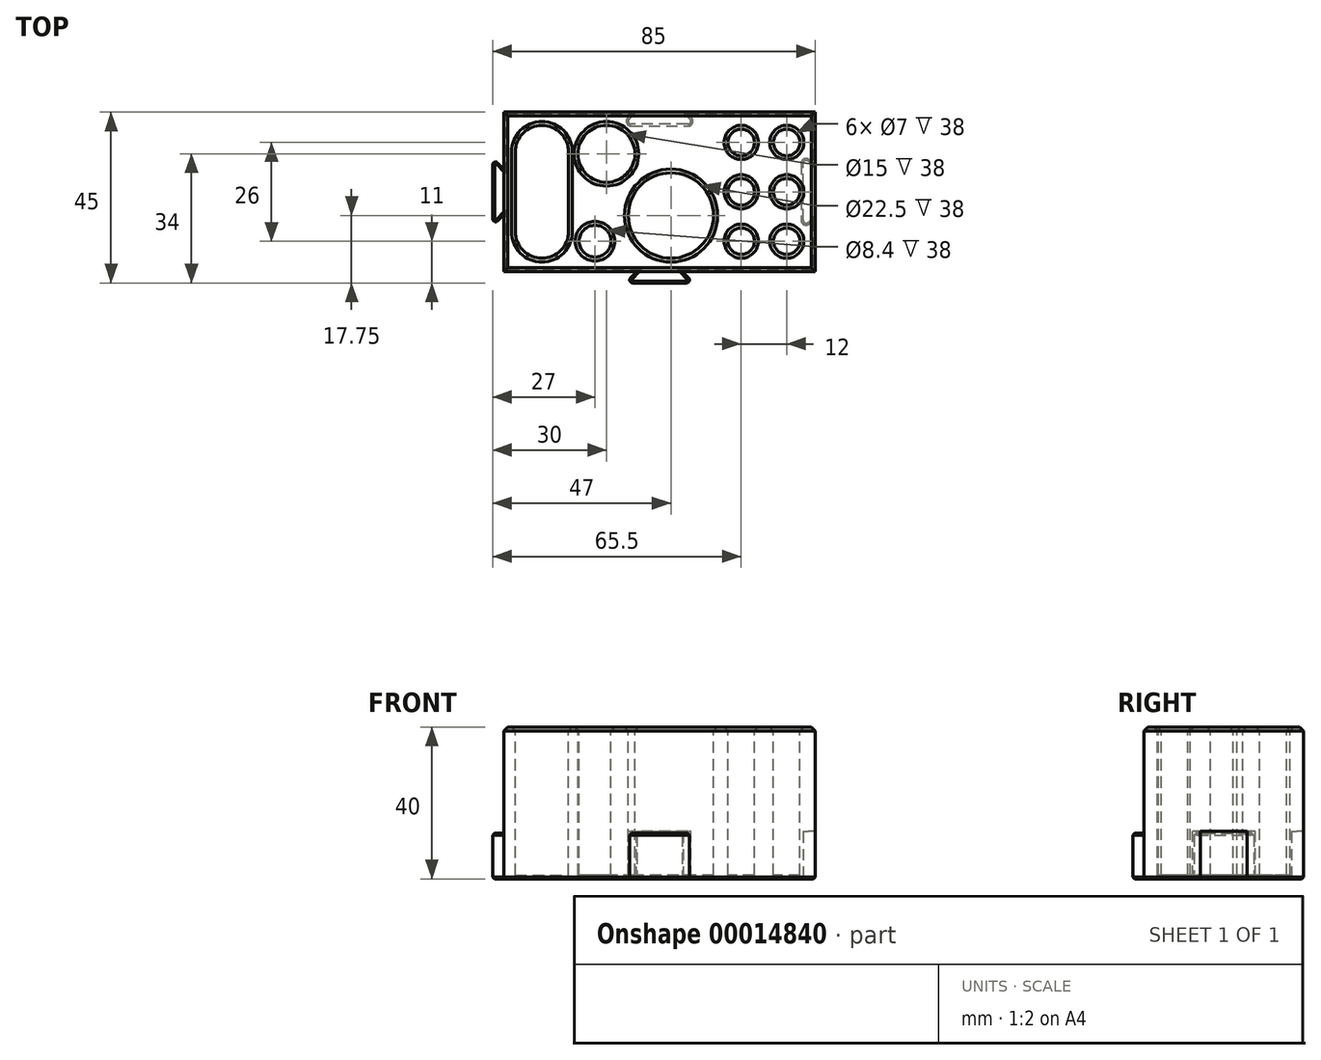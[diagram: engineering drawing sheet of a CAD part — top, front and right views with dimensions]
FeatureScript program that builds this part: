
annotation { "Feature Type Name" : "Feature", "Feature Type Description" : "" }
export const myFeature = defineFeature(function(context is Context, id is Id, definition is map)
    precondition{}
    {
        {
            var Q0;
            Q0=qCreatedBy(makeId("Top.planeOp"),FACE);
            var sketch = newSketch(context, id + "F0", { "sketchPlane" : qUnion([Q0])});
            skLineSegment(sketch, "E0.bottom", {"start": v(0, 0) * mm, "end": v(82, 0) * mm});
            skLineSegment(sketch, "E0.top", {"start": v(0, 42) * mm, "end": v(82, 42) * mm});
            skLineSegment(sketch, "E0.left", {"start": v(0, 0) * mm, "end": v(0, 42) * mm});
            skLineSegment(sketch, "E0.right", {"start": v(82, 0) * mm, "end": v(82, 42) * mm});
            skLineSegment(sketch, "E1", {"start": v(0, 21) * mm, "end": v(82, 21) * mm, "construction": true});
            skLineSegment(sketch, "E2", {"start": v(41, 42) * mm, "end": v(41, 0) * mm, "construction": true});
            skLineSegment(sketch, "E3", {"start": v(35, 0) * mm, "end": v(32, -3) * mm});
            skLineSegment(sketch, "E4", {"start": v(32, -3) * mm, "end": v(50, -3) * mm});
            skLineSegment(sketch, "E5", {"start": v(50, -3) * mm, "end": v(47, 0) * mm});
            skLineSegment(sketch, "E6", {"start": v(47.2, 42) * mm, "end": v(50.4, 38.8) * mm});
            skLineSegment(sketch, "E7", {"start": v(50.4, 38.8) * mm, "end": v(31.6, 38.8) * mm});
            skLineSegment(sketch, "E8", {"start": v(31.6, 38.8) * mm, "end": v(34.8, 42) * mm});
            skLineSegment(sketch, "E9", {"start": v(0, 15) * mm, "end": v(-3, 12) * mm});
            skLineSegment(sketch, "E10", {"start": v(-3, 12) * mm, "end": v(-3, 30) * mm});
            skLineSegment(sketch, "E11", {"start": v(-3, 30) * mm, "end": v(0, 27) * mm});
            skLineSegment(sketch, "E12", {"start": v(82, 14.8) * mm, "end": v(78.8, 11.6) * mm});
            skLineSegment(sketch, "E13", {"start": v(78.8, 11.6) * mm, "end": v(78.8, 30.4) * mm});
            skLineSegment(sketch, "E14", {"start": v(78.8, 30.4) * mm, "end": v(82, 27.2) * mm});
            skSolve(sketch);
        }
        {
            var Q0;
            {var subQ1=sQuery(id+"F0.wireOp",EDGE,"E6");Q0=makeQuery(id+"F0.imprint","IMPRINT",FACE,{"disambiguationData":[TD([[makeQuery(id+"F0.imprint","IMPRINT",EDGE,{"derivedFrom":subQ1}),-1.0]])]});}
            var Q1;
            {var subQ1=sQuery(id+"F0.wireOp",EDGE,"E12");Q1=makeQuery(id+"F0.imprint","IMPRINT",FACE,{"disambiguationData":[TD([[makeQuery(id+"F0.imprint","IMPRINT",EDGE,{"derivedFrom":subQ1}),-1.0]])]});}
            var Q2;
            {var subQ8=sQuery(id+"F0.wireOp",EDGE,"E6");Q2=makeQuery(id+"F0.imprint","IMPRINT",FACE,{"disambiguationData":[TD([[makeQuery(id+"F0.imprint","IMPRINT",EDGE,{"derivedFrom":subQ8}),1.0]])]});}
            extrude(context, id + "F1", {"entities" : qUnion([Q0, Q1, Q2]), "depth" : 40 * mm});
        }
        {
            var Q0;
            {var subQ1=sQuery(id+"F0.wireOp",EDGE,"E3");Q0=makeQuery(id+"F0.imprint","IMPRINT",FACE,{"disambiguationData":[TD([[makeQuery(id+"F0.imprint","IMPRINT",EDGE,{"derivedFrom":subQ1}),1.0]])]});}
            var Q1;
            {var subQ1=sQuery(id+"F0.wireOp",EDGE,"E9");Q1=makeQuery(id+"F0.imprint","IMPRINT",FACE,{"disambiguationData":[TD([[makeQuery(id+"F0.imprint","IMPRINT",EDGE,{"derivedFrom":subQ1}),-1.0]])]});}
            extrude(context, id + "F2", {"entities" : qUnion([Q0, Q1]), "operationType" : NewBodyOperationType.ADD, "depth" : 12 * mm});
        }
        {
            var Q0;
            {var subQ1=sQuery(id+"F0.wireOp",EDGE,"E6");Q0=makeQuery(id+"F0.imprint","IMPRINT",FACE,{"disambiguationData":[TD([[makeQuery(id+"F0.imprint","IMPRINT",EDGE,{"derivedFrom":subQ1}),-1.0]])]});}
            var Q1;
            {var subQ1=sQuery(id+"F0.wireOp",EDGE,"E12");Q1=makeQuery(id+"F0.imprint","IMPRINT",FACE,{"disambiguationData":[TD([[makeQuery(id+"F0.imprint","IMPRINT",EDGE,{"derivedFrom":subQ1}),-1.0]])]});}
            extrude(context, id + "F3", {"entities" : qUnion([Q0, Q1]), "operationType" : NewBodyOperationType.REMOVE, "depth" : 12.5 * mm});
        }
        {
            var Q0;
            Q0=makeQuery(id+"F3.boolean.opBoolean","COPY",EDGE,{"derivedFrom":makeQuery(id+"F3.opExtrude","SWEPT_EDGE",EDGE,{"disambiguationData":[OSD([sQuery(id+"F0.wireOp",EDGE,"E0.right"),sQuery(id+"F0.wireOp",EDGE,"E14")])]})});
            var Q1;
            Q1=makeQuery(id+"F3.boolean.opBoolean","COPY",EDGE,{"derivedFrom":makeQuery(id+"F3.opExtrude","SWEPT_EDGE",EDGE,{"disambiguationData":[OSD([sQuery(id+"F0.wireOp",EDGE,"E13"),sQuery(id+"F0.wireOp",EDGE,"E14")])]})});
            var Q2;
            Q2=makeQuery(id+"F3.boolean.opBoolean","COPY",EDGE,{"derivedFrom":makeQuery(id+"F3.opExtrude","SWEPT_EDGE",EDGE,{"disambiguationData":[OSD([sQuery(id+"F0.wireOp",EDGE,"E0.right"),sQuery(id+"F0.wireOp",EDGE,"E12")])]})});
            var Q3;
            Q3=makeQuery(id+"F2.opExtrude","SWEPT_EDGE",EDGE,{"disambiguationData":[OSD([sQuery(id+"F0.wireOp",EDGE,"E4"),sQuery(id+"F0.wireOp",EDGE,"E5")])]});
            var Q4;
            Q4=makeQuery(id+"F3.boolean.opBoolean","COPY",EDGE,{"derivedFrom":makeQuery(id+"F3.opExtrude","SWEPT_EDGE",EDGE,{"disambiguationData":[OSD([sQuery(id+"F0.wireOp",EDGE,"E12"),sQuery(id+"F0.wireOp",EDGE,"E13")])]})});
            var Q5;
            Q5=makeQuery(id+"F3.boolean.opBoolean","COPY",EDGE,{"derivedFrom":makeQuery(id+"F3.opExtrude","SWEPT_EDGE",EDGE,{"disambiguationData":[OSD([sQuery(id+"F0.wireOp",EDGE,"E0.top"),sQuery(id+"F0.wireOp",EDGE,"E8")])]})});
            var Q6;
            Q6=makeQuery(id+"F3.boolean.opBoolean","COPY",EDGE,{"derivedFrom":makeQuery(id+"F3.opExtrude","SWEPT_EDGE",EDGE,{"disambiguationData":[OSD([sQuery(id+"F0.wireOp",EDGE,"E0.top"),sQuery(id+"F0.wireOp",EDGE,"E6")])]})});
            var Q7;
            Q7=makeQuery(id+"F3.boolean.opBoolean","COPY",EDGE,{"derivedFrom":makeQuery(id+"F3.opExtrude","SWEPT_EDGE",EDGE,{"disambiguationData":[OSD([sQuery(id+"F0.wireOp",EDGE,"E7"),sQuery(id+"F0.wireOp",EDGE,"E8")])]})});
            var Q8;
            Q8=makeQuery(id+"F3.boolean.opBoolean","COPY",EDGE,{"derivedFrom":makeQuery(id+"F3.opExtrude","SWEPT_EDGE",EDGE,{"disambiguationData":[OSD([sQuery(id+"F0.wireOp",EDGE,"E6"),sQuery(id+"F0.wireOp",EDGE,"E7")])]})});
            var Q9;
            Q9=makeQuery(id+"F2.opExtrude","SWEPT_EDGE",EDGE,{"disambiguationData":[OSD([sQuery(id+"F0.wireOp",EDGE,"E10"),sQuery(id+"F0.wireOp",EDGE,"E11")])]});
            var Q10;
            Q10=makeQuery(id+"F2.opExtrude","SWEPT_EDGE",EDGE,{"disambiguationData":[OSD([sQuery(id+"F0.wireOp",EDGE,"E0.left"),sQuery(id+"F0.wireOp",EDGE,"E11")])]});
            var Q11;
            Q11=makeQuery(id+"F2.opExtrude","SWEPT_EDGE",EDGE,{"disambiguationData":[OSD([sQuery(id+"F0.wireOp",EDGE,"E0.left"),sQuery(id+"F0.wireOp",EDGE,"E9")])]});
            var Q12;
            Q12=makeQuery(id+"F2.opExtrude","SWEPT_EDGE",EDGE,{"disambiguationData":[OSD([sQuery(id+"F0.wireOp",EDGE,"E9"),sQuery(id+"F0.wireOp",EDGE,"E10")])]});
            var Q13;
            Q13=makeQuery(id+"F2.opExtrude","SWEPT_EDGE",EDGE,{"disambiguationData":[OSD([sQuery(id+"F0.wireOp",EDGE,"E3"),sQuery(id+"F0.wireOp",EDGE,"E4")])]});
            var Q14;
            Q14=makeQuery(id+"F2.opExtrude","SWEPT_EDGE",EDGE,{"disambiguationData":[OSD([sQuery(id+"F0.wireOp",EDGE,"E0.bottom"),sQuery(id+"F0.wireOp",EDGE,"E3")])]});
            var Q15;
            Q15=makeQuery(id+"F2.opExtrude","SWEPT_EDGE",EDGE,{"disambiguationData":[OSD([sQuery(id+"F0.wireOp",EDGE,"E0.bottom"),sQuery(id+"F0.wireOp",EDGE,"E5")])]});
            fillet(context, id + "F4", {"entities" : qUnion([Q0, Q1, Q2, Q3, Q4, Q5, Q6, Q7, Q8, Q9, Q10, Q11, Q12, Q13, Q14, Q15]), "radius" : .8 * mm, "tangentPropagation" : true, "allowEdgeOverflow" : false});
        }
        {
            var Q0;
            Q0=makeQuery(id+"F2.opExtrude","CAP_EDGE",EDGE,{"disambiguationData":[OSD([sQuery(id+"F0.wireOp",EDGE,"E4")])],"isStart":false});
            var Q1;
            Q1=makeQuery(id+"F2.opExtrude","CAP_EDGE",EDGE,{"disambiguationData":[OSD([sQuery(id+"F0.wireOp",EDGE,"E10")])],"isStart":false});
            chamfer(context, id + "F5", {"entities" : qUnion([Q0, Q1]), "width" : .5 * mm, "tangentPropagation" : true});
        }
        {
            var Q0;
            {var subQ0=sQuery(id+"F0.wireOp",EDGE,"E0.bottom");var subQ1=sQuery(id+"F0.wireOp",EDGE,"E0.left");Q0=makeQuery(id+"F2.boolean.opBoolean","MERGE",FACE,{"derivedFrom":[makeQuery(id+"F1.opExtrude","CAP_FACE",FACE,{"disambiguationData":[OSD([subQ0,sQuery(id+"F0.wireOp",EDGE,"E0.top"),subQ1,sQuery(id+"F0.wireOp",EDGE,"E0.right")])],"isStart":true}),makeQuery(id+"F2.opExtrude","CAP_FACE",FACE,{"disambiguationData":[OSD([subQ0,sQuery(id+"F0.wireOp",EDGE,"E3"),sQuery(id+"F0.wireOp",EDGE,"E4"),sQuery(id+"F0.wireOp",EDGE,"E5")])],"isStart":true}),makeQuery(id+"F2.opExtrude","CAP_FACE",FACE,{"disambiguationData":[OSD([subQ1,sQuery(id+"F0.wireOp",EDGE,"E9"),sQuery(id+"F0.wireOp",EDGE,"E10"),sQuery(id+"F0.wireOp",EDGE,"E11")])],"isStart":true})]});}
            chamfer(context, id + "F6", {"entities" : qUnion([Q0]), "width" : .5 * mm, "tangentPropagation" : true});
        }
        {
            var Q0;
            Q0=makeQuery(id+"F1.opExtrude","CAP_FACE",FACE,{"disambiguationData":[OSD([sQuery(id+"F0.wireOp",EDGE,"E0.bottom"),sQuery(id+"F0.wireOp",EDGE,"E0.top"),sQuery(id+"F0.wireOp",EDGE,"E0.left"),sQuery(id+"F0.wireOp",EDGE,"E0.right")])],"isStart":false});
            var sketch = newSketch(context, id + "F7", { "sketchPlane" : qUnion([Q0])});
            skLineSegment(sketch, "E15", {"start": v(3, 31.5) * mm, "end": v(3, 10.5) * mm});
            skLineSegment(sketch, "E16", {"start": v(17, 10.5) * mm, "end": v(17, 31.5) * mm});
            skArc(sketch, "E17", {"start": v(3, 10.5) * mm, "mid": v(10, 3.5) * mm, "end": v(17, 10.5) * mm});
            skArc(sketch, "E18", {"start": v(17, 31.5) * mm, "mid": v(10, 38.5) * mm, "end": v(3, 31.5) * mm});
            skLineSegment(sketch, "E19", {"start": v(0, 21) * mm, "end": v(82, 21) * mm, "construction": true});
            skCircle(sketch, "E20", {"center": v(24, 8) * mm, "radius": 4.2 * mm});
            skCircle(sketch, "E21", {"center": v(62.5, 21) * mm, "radius": 3.5 * mm});
            skCircle(sketch, "E22", {"center": v(62.5, 34) * mm, "radius": 3.5 * mm});
            skCircle(sketch, "E23", {"center": v(74.5, 21) * mm, "radius": 3.5 * mm});
            skCircle(sketch, "E24", {"center": v(74.5, 34) * mm, "radius": 3.5 * mm});
            skCircle(sketch, "E25", {"center": v(74.5, 8) * mm, "radius": 3.5 * mm});
            skCircle(sketch, "E26", {"center": v(62.5, 8) * mm, "radius": 3.5 * mm});
            skCircle(sketch, "E27", {"center": v(44, 14.75) * mm, "radius": 11.25 * mm});
            skCircle(sketch, "E28", {"center": v(27, 31) * mm, "radius": 7.5 * mm});
            skSolve(sketch);
        }
        {
            var Q0;
            Q0=makeQuery(id+"F7.imprint","IMPRINT",FACE,{"disambiguationData":[TD([[makeQuery(id+"F7.imprint","IMPRINT",EDGE,{"derivedFrom":sQuery(id+"F7.wireOp",EDGE,"E26")}),1.0]])]});
            var Q1;
            Q1=makeQuery(id+"F7.imprint","IMPRINT",FACE,{"disambiguationData":[TD([[makeQuery(id+"F7.imprint","IMPRINT",EDGE,{"derivedFrom":sQuery(id+"F7.wireOp",EDGE,"E21")}),1.0]])]});
            var Q2;
            Q2=makeQuery(id+"F7.imprint","IMPRINT",FACE,{"disambiguationData":[TD([[makeQuery(id+"F7.imprint","IMPRINT",EDGE,{"derivedFrom":sQuery(id+"F7.wireOp",EDGE,"E22")}),1.0]])]});
            var Q3;
            Q3=makeQuery(id+"F7.imprint","IMPRINT",FACE,{"disambiguationData":[TD([[makeQuery(id+"F7.imprint","IMPRINT",EDGE,{"derivedFrom":sQuery(id+"F7.wireOp",EDGE,"E24")}),1.0]])]});
            var Q4;
            Q4=makeQuery(id+"F7.imprint","IMPRINT",FACE,{"disambiguationData":[TD([[makeQuery(id+"F7.imprint","IMPRINT",EDGE,{"derivedFrom":sQuery(id+"F7.wireOp",EDGE,"E23")}),1.0]])]});
            var Q5;
            Q5=makeQuery(id+"F7.imprint","IMPRINT",FACE,{"disambiguationData":[TD([[makeQuery(id+"F7.imprint","IMPRINT",EDGE,{"derivedFrom":sQuery(id+"F7.wireOp",EDGE,"E25")}),1.0]])]});
            var Q6;
            Q6=makeQuery(id+"F7.imprint","IMPRINT",FACE,{"disambiguationData":[TD([[makeQuery(id+"F7.imprint","IMPRINT",EDGE,{"derivedFrom":sQuery(id+"F7.wireOp",EDGE,"E20")}),1.0]])]});
            var Q7;
            Q7=makeQuery(id+"F7.imprint","IMPRINT",FACE,{"disambiguationData":[TD([[makeQuery(id+"F7.imprint","IMPRINT",EDGE,{"derivedFrom":sQuery(id+"F7.wireOp",EDGE,"E15")}),1.0]])]});
            var Q8;
            Q8=makeQuery(id+"F7.imprint","IMPRINT",FACE,{"disambiguationData":[TD([[makeQuery(id+"F7.imprint","IMPRINT",EDGE,{"derivedFrom":sQuery(id+"F7.wireOp",EDGE,"E27")}),1.0]])]});
            var Q9;
            Q9=makeQuery(id+"F7.imprint","IMPRINT",FACE,{"disambiguationData":[TD([[makeQuery(id+"F7.imprint","IMPRINT",EDGE,{"derivedFrom":sQuery(id+"F7.wireOp",EDGE,"E28")}),1.0]])]});
            extrude(context, id + "F8", {"entities" : qUnion([Q0, Q1, Q2, Q3, Q4, Q5, Q6, Q7, Q8, Q9]), "operationType" : NewBodyOperationType.REMOVE, "oppositeDirection" : true, "depth" : 39 * mm});
        }
        {
            var Q0;
            Q0=makeQuery(id+"F1.opExtrude","CAP_FACE",FACE,{"disambiguationData":[OSD([sQuery(id+"F0.wireOp",EDGE,"E0.bottom"),sQuery(id+"F0.wireOp",EDGE,"E0.top"),sQuery(id+"F0.wireOp",EDGE,"E0.left"),sQuery(id+"F0.wireOp",EDGE,"E0.right")])],"isStart":false});
            chamfer(context, id + "F9", {"entities" : qUnion([Q0]), "width" : 1 * mm, "tangentPropagation" : true});
        }
    });
